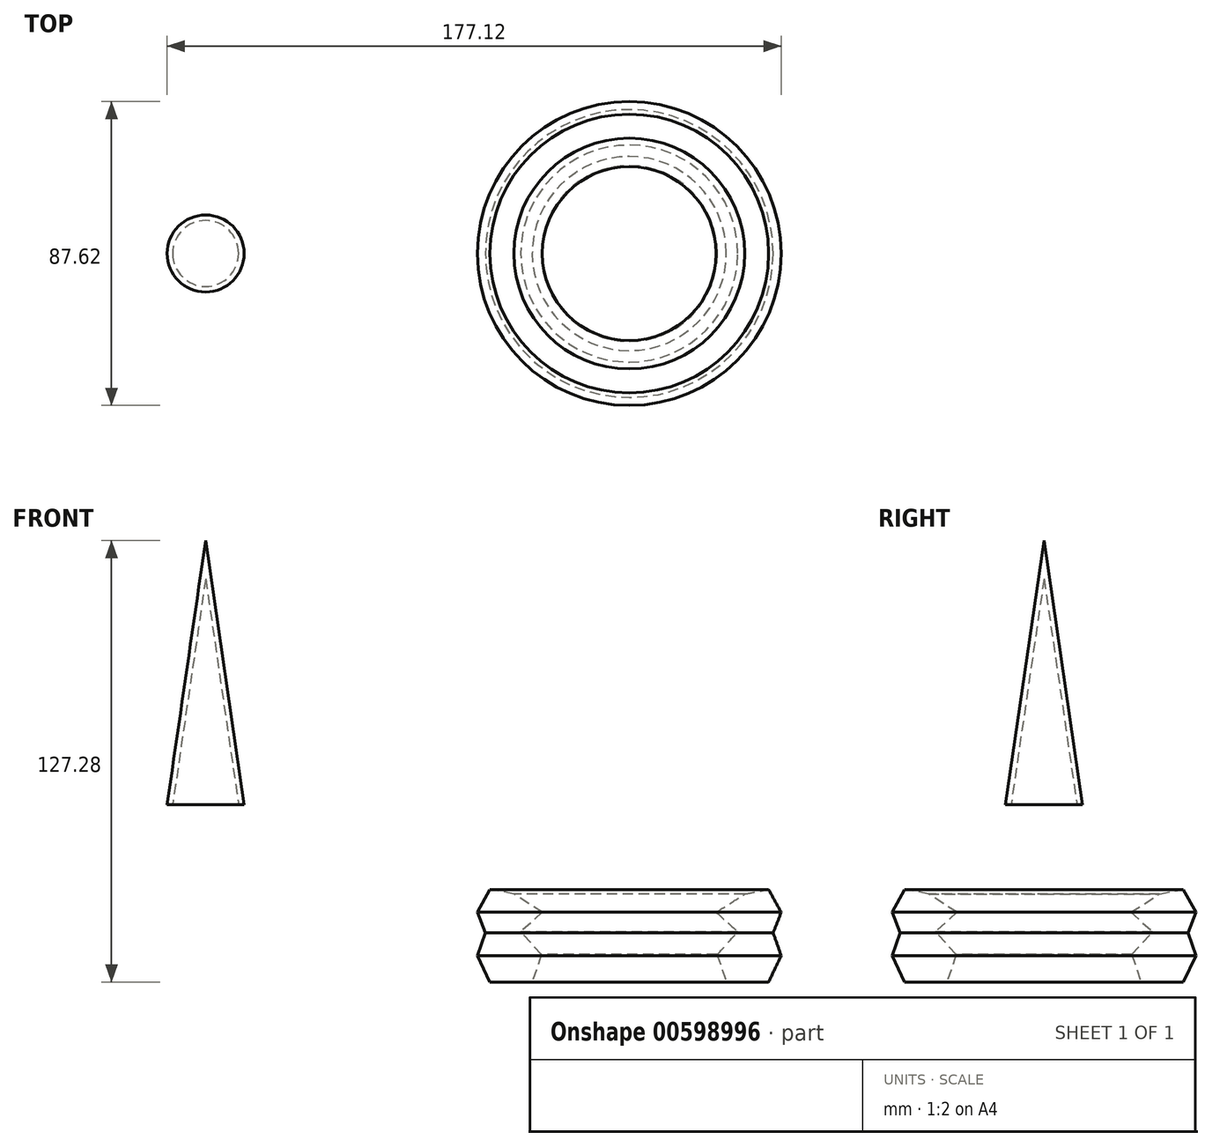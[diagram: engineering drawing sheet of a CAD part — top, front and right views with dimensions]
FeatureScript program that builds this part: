
annotation { "Feature Type Name" : "Feature", "Feature Type Description" : "" }
export const myFeature = defineFeature(function(context is Context, id is Id, definition is map)
    precondition{}
    {
        {
            var Q0;
            Q0=qCreatedBy(makeId("Front.planeOp"),FACE);
            var sketch = newSketch(context, id + "F0", { "sketchPlane" : qUnion([Q0])});
            skLineSegment(sketch, "E0", {"start": v(-40.96, 6.97) * mm, "end": v(-39.36, 6.97) * mm});
            skLineSegment(sketch, "E1", {"start": v(-29.85, 83.17) * mm, "end": v(-40.96, 6.97) * mm});
            skLineSegment(sketch, "E2.0", {"start": v(-29.85, 72.17) * mm, "end": v(-39.36, 6.97) * mm});
            skLineSegment(sketch, "E3", {"start": v(-29.85, 83.17) * mm, "end": v(-29.85, 72.17) * mm});
            skSolve(sketch);
        }
        {
            var Q0;
            Q0=makeQuery(id+"F0.imprint","IMPRINT",FACE,{"disambiguationData":[TD([[makeQuery(id+"F0.imprint","IMPRINT",EDGE,{"derivedFrom":sQuery(id+"F0.wireOp",EDGE,"E0")}),1.0]])]});
            var Q1;
            Q1=sQuery(id+"F0.wireOp",EDGE,"E3");
            revolve(context, id + "F1", {"entities" : qUnion([Q0]), "axis" : qUnion([Q1]), "revolveType" : RevolveType.FULL});
        }
        {
            var Q0;
            Q0=qCreatedBy(makeId("Front.planeOp"),FACE);
            var sketch = newSketch(context, id + "F2", { "sketchPlane" : qUnion([Q0])});
            skLineSegment(sketch, "E4", {"start": v(52.16, -17.43) * mm, "end": v(48.54, -24.02) * mm});
            skLineSegment(sketch, "E5", {"start": v(48.54, -24.02) * mm, "end": v(50.84, -29.95) * mm});
            skLineSegment(sketch, "E6", {"start": v(50.84, -29.95) * mm, "end": v(48.54, -36.54) * mm});
            skLineSegment(sketch, "E7", {"start": v(48.54, -36.54) * mm, "end": v(52.16, -44.11) * mm});
            skLineSegment(sketch, "E8", {"start": v(52.16, -44.11) * mm, "end": v(64.35, -44.11) * mm});
            skLineSegment(sketch, "E9", {"start": v(64.35, -44.11) * mm, "end": v(66.98, -36.2) * mm});
            skLineSegment(sketch, "E10", {"start": v(66.98, -36.2) * mm, "end": v(61.05, -29.62) * mm});
            skLineSegment(sketch, "E11", {"start": v(61.05, -29.62) * mm, "end": v(67.28, -24.02) * mm});
            skLineSegment(sketch, "E12", {"start": v(67.28, -24.02) * mm, "end": v(59.07, -18.75) * mm});
            skLineSegment(sketch, "E13", {"start": v(59.07, -18.75) * mm, "end": v(52.16, -17.43) * mm});
            skLineSegment(sketch, "E14", {"start": v(92.35, -24.02) * mm, "end": v(92.35, -41.48) * mm});
            skSolve(sketch);
        }
        {
            var Q0;
            Q0=makeQuery(id+"F2.imprint","IMPRINT",FACE,{"disambiguationData":[TD([[makeQuery(id+"F2.imprint","IMPRINT",EDGE,{"derivedFrom":sQuery(id+"F2.wireOp",EDGE,"E4")}),1.0]])]});
            var Q1;
            Q1=sQuery(id+"F2.wireOp",EDGE,"E14");
            revolve(context, id + "F3", {"entities" : qUnion([Q0]), "axis" : qUnion([Q1]), "revolveType" : RevolveType.FULL});
        }
    });
